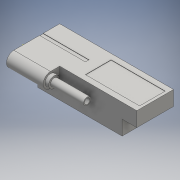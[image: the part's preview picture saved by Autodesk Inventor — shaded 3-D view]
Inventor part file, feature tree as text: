
AUTODESK INVENTOR PART (.ipt)
format: ipt  version: 2016 (Build 200138000, 138)  size: 173,056 bytes
history: native  units: mm
features: sketch x8, extrude x7, other x1, chamfer x1
ambient origin geometry x8: Origin, YZ Plane, XZ Plane, XY Plane, X Axis, Y Axis, Z Axis, Center Point
bodies: Body1 (feature_tree)
feature tree (17):
  other  "ソリッド1"
  extrude  "押し出し1"  Depth=62.0mm
  extrude  "押し出し2"  Depth=20.0mm
  extrude  "押し出し3"  Depth=8.0mm TaperAngle=0.0deg
  extrude  "押し出し4"  Depth=1.0mm
  extrude  "押し出し5"  Depth=4.0mm
  chamfer  "面取り1"  Distance=6.0mm
  extrude  "押し出し6"  Depth=20.0mm TaperAngle=0.0deg
  extrude  "押し出し8"  Depth=2.0mm TaperAngle=0.0deg
  sketch  "スケッチ8"
  sketch  "スケッチ1"
  sketch  "スケッチ2"
  sketch  "スケッチ3"
  sketch  "スケッチ4"
  sketch  "スケッチ5"
  sketch  "スケッチ6"
  sketch  "スケッチ7"
